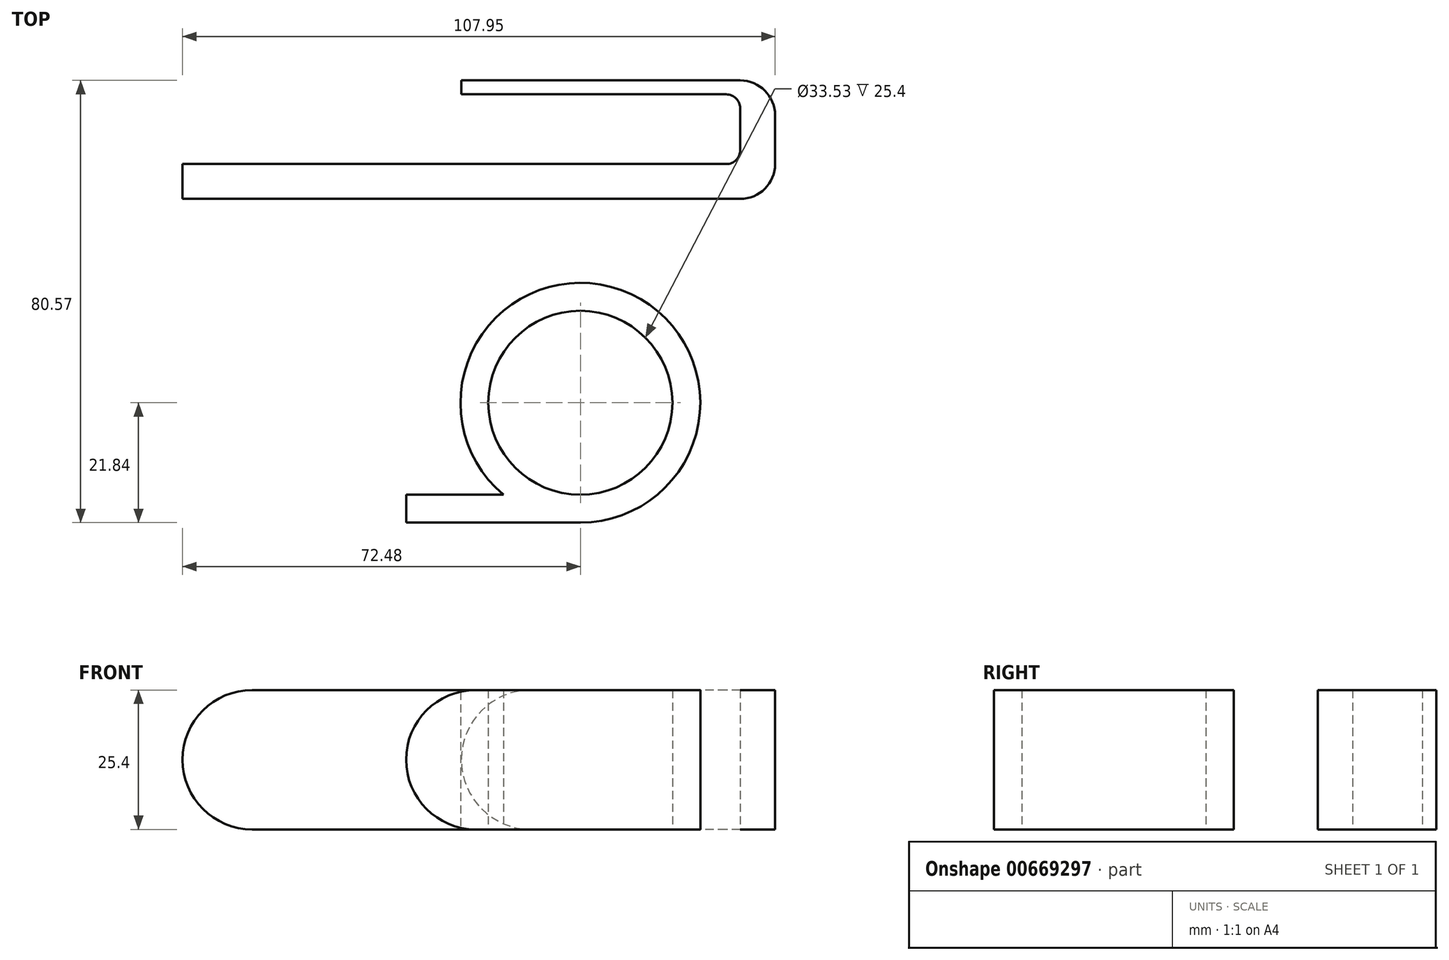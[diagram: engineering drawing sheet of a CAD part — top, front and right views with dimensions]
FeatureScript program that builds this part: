
annotation { "Feature Type Name" : "Feature", "Feature Type Description" : "" }
export const myFeature = defineFeature(function(context is Context, id is Id, definition is map)
    precondition{}
    {
        {
            var Q0;
            Q0=qCreatedBy(makeId("Top.planeOp"),FACE);
            var sketch = newSketch(context, id + "F0", { "sketchPlane" : qUnion([Q0])});
            skCircle(sketch, "E0", {"center": v(0, 0) * mm, "radius": 21.84 * mm});
            skCircle(sketch, "E1", {"center": v(0, 0) * mm, "radius": 16.76 * mm});
            skSolve(sketch);
        }
        {
            var Q0;
            Q0 = qSketchRegion(id + "F0", true);
            extrude(context, id + "F1", {"entities" : qUnion([Q0]), "depth" : 25.4 * mm, "offsetDistance" : 25.4 * mm});
        }
        {
            var Q0;
            Q0=qCreatedBy(makeId("Front.planeOp"),FACE);
            cPlane(context, id + "F2", {"entities" : qUnion([Q0]), "cplaneType" : CPlaneType.OFFSET, "offset" : 21.84 * mm, "width" : 152.4 * mm, "height" : 152.4 * mm});
        }
        {
            var Q0;
            Q0=qCreatedBy(id+"F2.planeOp",FACE);
            var sketch = newSketch(context, id + "F3", { "sketchPlane" : qUnion([Q0])});
            skLineSegment(sketch, "E2", {"start": v(0, 0) * mm, "end": v(-19.05, 0) * mm});
            skLineSegment(sketch, "E3", {"start": v(-19.05, 0) * mm, "end": v(-19.05, 25.4) * mm});
            skLineSegment(sketch, "E4", {"start": v(-19.05, 25.4) * mm, "end": v(0, 25.4) * mm});
            skLineSegment(sketch, "E5", {"start": v(0, 25.4) * mm, "end": v(0, 0) * mm});
            skArc(sketch, "E6", {"start": v(-19.05, 25.4) * mm, "mid": v(-31.75, 12.7) * mm, "end": v(-19.05, 0) * mm});
            skSolve(sketch);
        }
        {
            var Q0;
            Q0=makeQuery(id+"F3.imprint","IMPRINT",FACE,{"disambiguationData":[TD([[makeQuery(id+"F3.imprint","IMPRINT",EDGE,{"derivedFrom":sQuery(id+"F3.wireOp",EDGE,"E2")}),-1.0]])]});
            var Q1;
            Q1=makeQuery(id+"F3.imprint","IMPRINT",FACE,{"disambiguationData":[TD([[makeQuery(id+"F3.imprint","IMPRINT",EDGE,{"derivedFrom":sQuery(id+"F3.wireOp",EDGE,"E3")}),1.0]])]});
            extrude(context, id + "F4", {"entities" : qUnion([Q0, Q1]), "operationType" : NewBodyOperationType.ADD, "oppositeDirection" : true, "depth" : 5.08 * mm, "offsetDistance" : 25.4 * mm});
        }
        {
            var Q0;
            Q0=qCreatedBy(makeId("Top.planeOp"),FACE);
            var sketch = newSketch(context, id + "F5", { "sketchPlane" : qUnion([Q0])});
            skLineSegment(sketch, "E7.bottom", {"start": v(26.58, 43.49) * mm, "end": v(-72.48, 43.49) * mm});
            skLineSegment(sketch, "E7.top", {"start": v(29.12, 37.14) * mm, "end": v(-72.48, 37.14) * mm});
            skLineSegment(sketch, "E7.right", {"start": v(-72.48, 43.49) * mm, "end": v(-72.48, 37.14) * mm});
            skLineSegment(sketch, "E8.left", {"start": v(35.47, 43.49) * mm, "end": v(35.47, 52.38) * mm});
            skLineSegment(sketch, "E8.right", {"start": v(29.12, 46.03) * mm, "end": v(29.12, 53.65) * mm});
            skLineSegment(sketch, "E9.bottom", {"start": v(29.12, 58.73) * mm, "end": v(-21.68, 58.73) * mm});
            skLineSegment(sketch, "E9.top", {"start": v(26.58, 56.19) * mm, "end": v(-21.68, 56.19) * mm});
            skLineSegment(sketch, "E9.right", {"start": v(-21.68, 58.73) * mm, "end": v(-21.68, 56.19) * mm});
            skArc(sketch, "E10.filletArc", {"start": v(29.12, 53.65) * mm, "mid": v(28.37, 55.45) * mm, "end": v(26.58, 56.19) * mm});
            skArc(sketch, "E11.filletArc", {"start": v(26.58, 43.49) * mm, "mid": v(28.37, 44.23) * mm, "end": v(29.12, 46.03) * mm});
            skPoint(sketch, "E12.visualSharp", {"position": v(35.47, 58.73) * mm});
            skArc(sketch, "E12.filletArc", {"start": v(35.47, 52.38) * mm, "mid": v(33.6, 56.87) * mm, "end": v(29.12, 58.73) * mm});
            skPoint(sketch, "E13.visualSharp", {"position": v(35.47, 37.14) * mm});
            skArc(sketch, "E13.filletArc", {"start": v(29.12, 37.14) * mm, "mid": v(33.6, 39) * mm, "end": v(35.47, 43.49) * mm});
            skSolve(sketch);
        }
        {
            var Q0;
            Q0 = qSketchRegion(id + "F5", true);
            extrude(context, id + "F6", {"entities" : qUnion([Q0]), "depth" : 25.4 * mm, "offsetDistance" : 25.4 * mm});
        }
        {
            var Q0;
            Q0=makeQuery(id+"F6.opExtrude","CAP_EDGE",EDGE,{"disambiguationData":[OSD([sQuery(id+"F5.wireOp",EDGE,"E7.right")])],"isStart":false});
            var Q1;
            Q1=makeQuery(id+"F6.opExtrude","CAP_EDGE",EDGE,{"disambiguationData":[OSD([sQuery(id+"F5.wireOp",EDGE,"E7.right")])],"isStart":true});
            var Q2;
            Q2=makeQuery(id+"F6.opExtrude","CAP_EDGE",EDGE,{"disambiguationData":[OSD([sQuery(id+"F5.wireOp",EDGE,"E9.right")])],"isStart":false});
            var Q3;
            Q3=makeQuery(id+"F6.opExtrude","CAP_EDGE",EDGE,{"disambiguationData":[OSD([sQuery(id+"F5.wireOp",EDGE,"E9.right")])],"isStart":true});
            fillet(context, id + "F7", {"entities" : qUnion([Q0, Q1, Q2, Q3]), "radius" : 12.7 * mm, "tangentPropagation" : true, "allowEdgeOverflow" : false});
        }
    });
